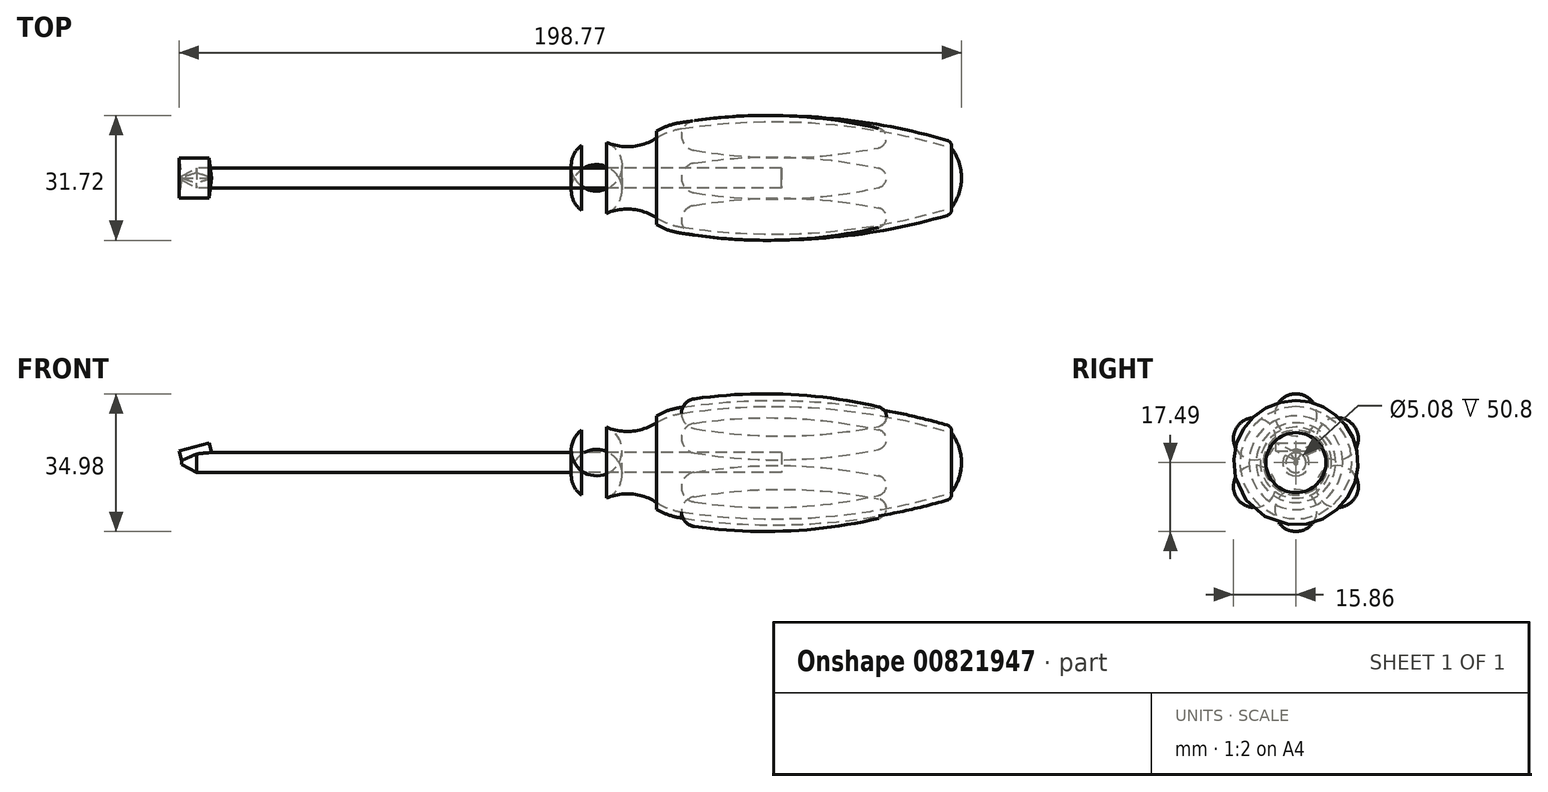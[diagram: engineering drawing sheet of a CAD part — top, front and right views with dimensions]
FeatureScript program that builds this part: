
annotation { "Feature Type Name" : "Feature", "Feature Type Description" : "" }
export const myFeature = defineFeature(function(context is Context, id is Id, definition is map)
    precondition{}
    {
        {
            var Q0;
            Q0=qCreatedBy(makeId("Front.planeOp"),FACE);
            var sketch = newSketch(context, id + "F0", { "sketchPlane" : qUnion([Q0])});
            skLineSegment(sketch, "E0", {"start": v(-101.6, 0) * mm, "end": v(96.52, 0) * mm});
            skLineSegment(sketch, "E1", {"start": v(96.52, 0) * mm, "end": v(117.55, 0) * mm, "construction": true});
            skLineSegment(sketch, "E2", {"start": v(50.8, 2.54) * mm, "end": v(-97.8, 2.54) * mm});
            skLineSegment(sketch, "E3", {"start": v(-101.6, 0.5) * mm, "end": v(-101.6, 0) * mm});
            skLineSegment(sketch, "E4", {"start": v(0, 2.54) * mm, "end": v(0, 8.25) * mm});
            skArc(sketch, "E5", {"start": v(6.35, 9.02) * mm, "mid": v(3.07, 9.48) * mm, "end": v(0, 8.25) * mm});
            skArc(sketch, "E6", {"start": v(6.35, 9.02) * mm, "mid": v(12.84, 7.99) * mm, "end": v(19.05, 10.11) * mm});
            skArc(sketch, "E7", {"start": v(25.4, 12.52) * mm, "mid": v(22.1, 11.65) * mm, "end": v(19.05, 10.11) * mm});
            skArc(sketch, "E8", {"start": v(93.98, 7.62) * mm, "mid": v(59.96, 13.9) * mm, "end": v(25.4, 12.52) * mm});
            skArc(sketch, "E9", {"start": v(96.52, 0) * mm, "mid": v(95.87, 4.02) * mm, "end": v(93.98, 7.62) * mm});
            skArc(sketch, "E10.0", {"start": v(25.17, 14.02) * mm, "mid": v(22.01, 13.24) * mm, "end": v(19.05, 11.9) * mm});
            skArc(sketch, "E10.1", {"start": v(92.95, 9.52) * mm, "mid": v(59.3, 15.46) * mm, "end": v(25.17, 14.02) * mm});
            skLineSegment(sketch, "E11", {"start": v(19.05, 11.9) * mm, "end": v(19.05, 10.11) * mm});
            skArc(sketch, "E12", {"start": v(93.98, 7.62) * mm, "mid": v(93.86, 8.78) * mm, "end": v(92.95, 9.52) * mm});
            skPoint(sketch, "E13.orphan", {"position": v(0, 0) * mm});
            skLineSegment(sketch, "E14", {"start": v(50.8, 2.54) * mm, "end": v(50.8, 0) * mm});
            skLineSegment(sketch, "E15", {"start": v(-101.6, 0.5) * mm, "end": v(-97.8, 2.54) * mm});
            skPoint(sketch, "E16.orphan", {"position": v(-101.6, 2.54) * mm});
            skSolve(sketch);
        }
        {
            var Q0;
            Q0=qCreatedBy(makeId("Front.planeOp"),FACE);
            var sketch = newSketch(context, id + "F1", { "sketchPlane" : qUnion([Q0])});
            skLineSegment(sketch, "E17", {"start": v(25.4, 12.52) * mm, "end": v(77.47, 11.64) * mm});
            skArc(sketch, "E18", {"start": v(28.67, 16.22) * mm, "mid": v(26.35, 14.97) * mm, "end": v(25.4, 12.52) * mm});
            skArc(sketch, "E19", {"start": v(77.47, 11.64) * mm, "mid": v(76.93, 13.25) * mm, "end": v(75.5, 14.16) * mm});
            skArc(sketch, "E20", {"start": v(75.5, 14.16) * mm, "mid": v(52.19, 17.37) * mm, "end": v(28.67, 16.22) * mm});
            skSolve(sketch);
        }
        {
            var Q0;
            Q0=qCreatedBy(makeId("Front.planeOp"),FACE);
            var sketch = newSketch(context, id + "F2", { "sketchPlane" : qUnion([Q0])});
            skLineSegment(sketch, "E21", {"start": v(-101.6, 0.5) * mm, "end": v(-93.98, 2.54) * mm});
            skSolve(sketch);
        }
        {
            var Q0;
            Q0=sQuery(id+"F2.wireOp",VERTEX,"E21.start");
            var Q1;
            Q1=sQuery(id+"F2.wireOp",EDGE,"E21");
            cPlane(context, id + "F3", {"entities" : qUnion([Q0, Q1]), "cplaneType" : CPlaneType.LINE_POINT, "offset" : 25.4 * mm, "width" : 152.4 * mm, "height" : 152.4 * mm});
        }
        {
            var Q0;
            Q0=qCreatedBy(id+"F3.planeOp",FACE);
            var sketch = newSketch(context, id + "F4", { "sketchPlane" : qUnion([Q0])});
            skLineSegment(sketch, "E22", {"start": v(5.08, 29.2) * mm, "end": v(0, 26.67) * mm});
            skLineSegment(sketch, "E23", {"start": v(0, 26.67) * mm, "end": v(-5.08, 29.2) * mm});
            skLineSegment(sketch, "E24", {"start": v(-5.08, 29.2) * mm, "end": v(5.08, 29.2) * mm});
            skLineSegment(sketch, "E25", {"start": v(0, 29.2) * mm, "end": v(0, 26.67) * mm, "construction": true});
            skSolve(sketch);
        }
        {
            var Q0;
            {var subQ0=sQuery(id+"F0.wireOp",EDGE,"E4");Q0=makeQuery(id+"F0.imprint","IMPRINT",FACE,{"disambiguationData":[TD([[makeQuery(id+"F0.imprint","IMPRINT",EDGE,{"derivedFrom":subQ0}),-1.0]])]});}
            var Q1;
            Q1=sQuery(id+"F0.wireOp",EDGE,"E1");
            revolve(context, id + "F5", {"surfaceOperationType" : NewSurfaceOperationType.NEW, "entities" : qUnion([Q0]), "axis" : qUnion([Q1]), "revolveType" : RevolveType.FULL});
        }
        {
            var Q0;
            Q0=makeQuery(id+"F0.imprint","IMPRINT",FACE,{"disambiguationData":[TD([[makeQuery(id+"F0.imprint","IMPRINT",EDGE,{"derivedFrom":sQuery(id+"F0.wireOp",EDGE,"E7")}),-1.0]])]});
            var Q1;
            Q1=sQuery(id+"F0.wireOp",EDGE,"E1");
            revolve(context, id + "F6", {"surfaceOperationType" : NewSurfaceOperationType.NEW, "entities" : qUnion([Q0]), "axis" : qUnion([Q1]), "revolveType" : RevolveType.FULL});
        }
        {
            var Q0;
            Q0=makeQuery(id+"F1.imprint","IMPRINT",FACE,{"disambiguationData":[TD([[makeQuery(id+"F1.imprint","IMPRINT",EDGE,{"derivedFrom":sQuery(id+"F1.wireOp",EDGE,"E17")}),1.0]])]});
            var Q1;
            Q1=sQuery(id+"F1.wireOp",EDGE,"E17");
            revolve(context, id + "F7", {"surfaceOperationType" : NewSurfaceOperationType.NEW, "entities" : qUnion([Q0]), "axis" : qUnion([Q1]), "revolveType" : RevolveType.FULL});
        }
        {
            var Q0;
            Q0=makeQuery(id+"F7.opRevolve","SWEPT_BODY",BODY,{"disambiguationData":[OSD([sQuery(id+"F1.wireOp",EDGE,"E17"),sQuery(id+"F1.wireOp",EDGE,"E18"),sQuery(id+"F1.wireOp",EDGE,"E19"),sQuery(id+"F1.wireOp",EDGE,"E20")])]});
            var Q1;
            Q1=sQuery(id+"F0.wireOp",EDGE,"E1");
            circularPattern(context, id + "F8", {"entities" : qUnion([Q0]), "axis" : qUnion([Q1]), "angle" : 360 * degree, "instanceCount" : 6, "equalSpace" : true});
        }
        {
            var Q0;
            {var subQ0=sQuery(id+"F0.wireOp",EDGE,"E3");Q0=makeQuery(id+"F0.imprint","IMPRINT",FACE,{"disambiguationData":[TD([[makeQuery(id+"F0.imprint","IMPRINT",EDGE,{"derivedFrom":subQ0}),1.0]])]});}
            var Q1;
            Q1=sQuery(id+"F0.wireOp",EDGE,"E1");
            revolve(context, id + "F9", {"surfaceOperationType" : NewSurfaceOperationType.NEW, "entities" : qUnion([Q0]), "axis" : qUnion([Q1]), "revolveType" : RevolveType.FULL});
        }
        {
            var Q0;
            Q0=makeQuery(id+"F4.imprint","IMPRINT",FACE,{"disambiguationData":[TD([[makeQuery(id+"F4.imprint","IMPRINT",EDGE,{"derivedFrom":sQuery(id+"F4.wireOp",EDGE,"E22")}),-1.0]])]});
            var Q1;
            Q1=qConstructionFilter(qBodyType(qCreatedBy(id+"F2",EDGE),BodyType.WIRE),ConstructionObject.NO);
            sweep(context, id + "F10", {"operationType" : NewBodyOperationType.REMOVE, "profiles" : qUnion([Q0]), "path" : qUnion([Q1])});
        }
        {
            var Q0;
            Q0=makeQuery(id+"F4.imprint","IMPRINT",FACE,{"disambiguationData":[TD([[makeQuery(id+"F4.imprint","IMPRINT",EDGE,{"derivedFrom":sQuery(id+"F4.wireOp",EDGE,"E22")}),-1.0]])]});
            var Q1;
            Q1=qConstructionFilter(qBodyType(qCreatedBy(id+"F2",EDGE),BodyType.WIRE),ConstructionObject.NO);
            sweep(context, id + "F11", {"profiles" : qUnion([Q0]), "path" : qUnion([Q1])});
        }
    });
